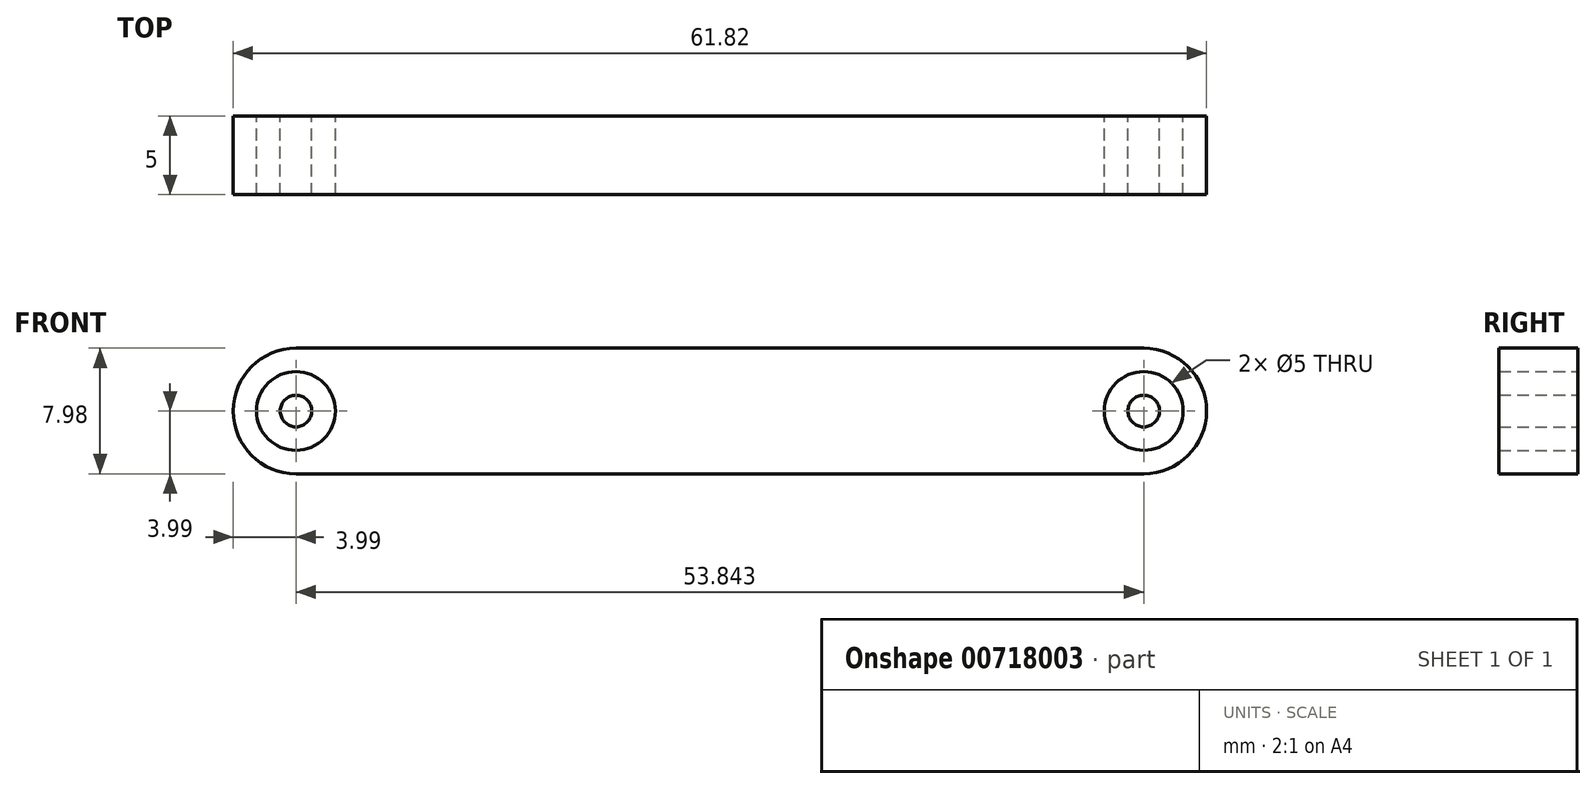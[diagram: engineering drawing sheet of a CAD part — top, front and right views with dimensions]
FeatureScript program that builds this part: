
annotation { "Feature Type Name" : "Feature", "Feature Type Description" : "" }
export const myFeature = defineFeature(function(context is Context, id is Id, definition is map)
    precondition{}
    {
        {
            var Q0;
            Q0=qCreatedBy(makeId("Front.planeOp"),FACE);
            var sketch = newSketch(context, id + "F0", { "sketchPlane" : qUnion([Q0])});
            skCircle(sketch, "E0", {"center": v(0, 0) * mm, "radius": 3.99 * mm});
            skCircle(sketch, "E1", {"center": v(53.84, 0) * mm, "radius": 3.99 * mm});
            skCircle(sketch, "E2", {"center": v(53.84, 0) * mm, "radius": 1 * mm});
            skCircle(sketch, "E3", {"center": v(0, 0) * mm, "radius": 1 * mm});
            skCircle(sketch, "E4", {"center": v(0, 0) * mm, "radius": 2.5 * mm});
            skCircle(sketch, "E5", {"center": v(53.84, 0) * mm, "radius": 2.5 * mm});
            skLineSegment(sketch, "E6", {"start": v(53.84, -3.99) * mm, "end": v(0, -3.99) * mm});
            skLineSegment(sketch, "E7", {"start": v(0, 3.99) * mm, "end": v(53.84, 3.99) * mm});
            skSolve(sketch);
        }
        {
            var Q0;
            Q0 = qSketchRegion(id + "F0", true);
            var Q1;
            Q1=makeQuery(id+"F0.imprint","IMPRINT",FACE,{"disambiguationData":[TD([[makeQuery(id+"F0.imprint","IMPRINT",EDGE,{"derivedFrom":sQuery(id+"F0.wireOp",EDGE,"E0")}),1.0]])]});
            var Q2;
            Q2=makeQuery(id+"F0.imprint","IMPRINT",FACE,{"disambiguationData":[TD([[makeQuery(id+"F0.imprint","IMPRINT",EDGE,{"derivedFrom":sQuery(id+"F0.wireOp",EDGE,"E1")}),1.0]])]});
            var Q3;
            Q3=makeQuery(id+"F0.imprint","IMPRINT",FACE,{"disambiguationData":[TD([[makeQuery(id+"F0.imprint","IMPRINT",EDGE,{"derivedFrom":sQuery(id+"F0.wireOp",EDGE,"E3")}),1.0]])]});
            var Q4;
            Q4=makeQuery(id+"F0.imprint","IMPRINT",FACE,{"disambiguationData":[TD([[makeQuery(id+"F0.imprint","IMPRINT",EDGE,{"derivedFrom":sQuery(id+"F0.wireOp",EDGE,"E2")}),1.0]])]});
            extrude(context, id + "F1", {"entities" : qUnion([Q0, Q1, Q2, Q3, Q4]), "depth" : 5 * mm, "offsetDistance" : 25 * mm});
        }
    });
